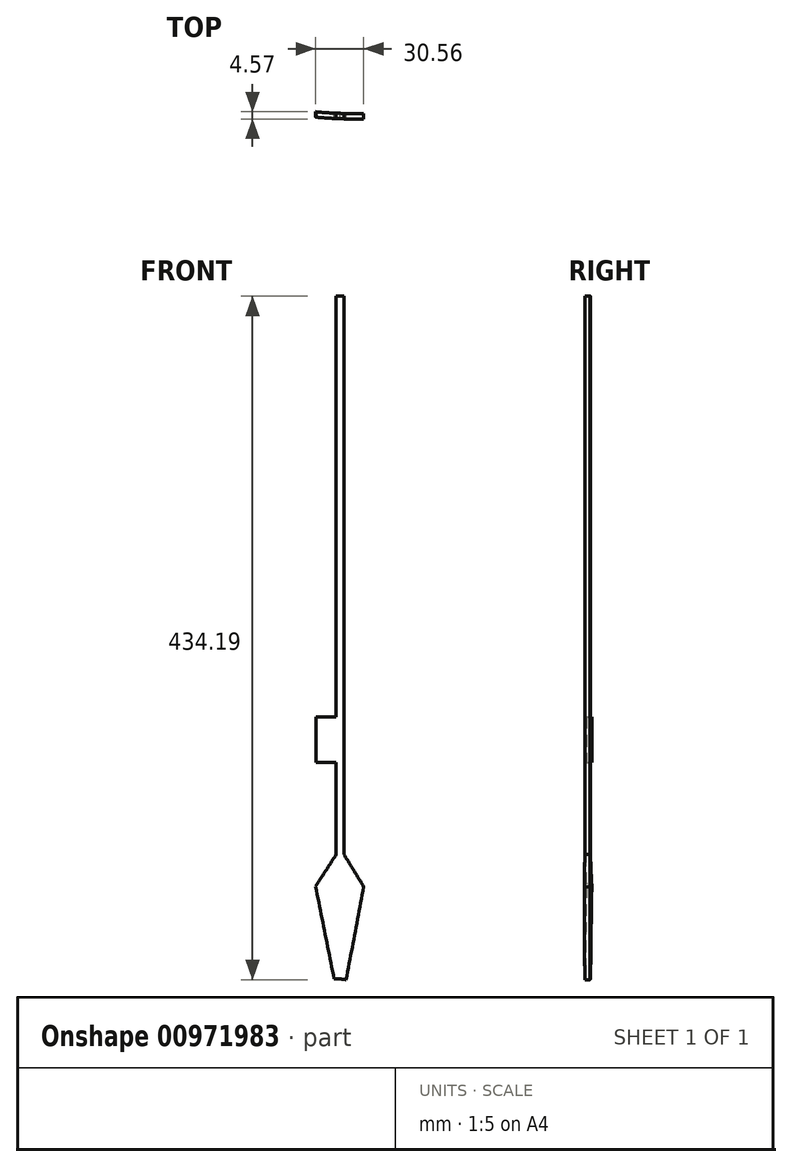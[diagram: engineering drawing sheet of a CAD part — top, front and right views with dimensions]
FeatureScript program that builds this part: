
annotation { "Feature Type Name" : "Feature", "Feature Type Description" : "" }
export const myFeature = defineFeature(function(context is Context, id is Id, definition is map)
    precondition{}
    {
        {
            var Q0;
            Q0=qCreatedBy(makeId("Front.planeOp"),FACE);
            var sketch = newSketch(context, id + "F0", { "sketchPlane" : qUnion([Q0])});
            skLineSegment(sketch, "E0.bottom", {"start": v(-1.3, 3.4) * mm, "end": v(-0.07, 3.4) * mm});
            skLineSegment(sketch, "E0.top", {"start": v(-1.3, -85.17) * mm, "end": v(-0.07, -85.17) * mm});
            skLineSegment(sketch, "E0.left", {"start": v(-1.3, 3.4) * mm, "end": v(-1.3, -85.17) * mm});
            skLineSegment(sketch, "E0.right", {"start": v(-0.07, 3.4) * mm, "end": v(-0.07, -85.17) * mm});
            skLineSegment(sketch, "E1", {"start": v(-1.3, -85.17) * mm, "end": v(-4.57, -90.2) * mm});
            skLineSegment(sketch, "E2", {"start": v(-0.07, -85.17) * mm, "end": v(3.07, -90.29) * mm});
            skLineSegment(sketch, "E3", {"start": v(-4.57, -90.2) * mm, "end": v(-1.63, -104.91) * mm});
            skLineSegment(sketch, "E4", {"start": v(-0.68, -85.17) * mm, "end": v(-0.68, -107.5) * mm});
            skLineSegment(sketch, "E5", {"start": v(3.07, -90.29) * mm, "end": v(0.28, -105.04) * mm});
            skLineSegment(sketch, "E6", {"start": v(-1.63, -104.91) * mm, "end": v(-0.68, -104.91) * mm});
            skLineSegment(sketch, "E7", {"start": v(0.28, -105.04) * mm, "end": v(-0.68, -104.91) * mm});
            skFitSpline(sketch, "E8", {"points": [v(-1.63, -104.91) * mm, v(-0.68, -107.5) * mm, v(0.28, -105.04) * mm], "startDerivative": vector(1.88, -7.65) * mm, "endDerivative": vector(1.95, 7.45) * mm});
            skLineSegment(sketch, "E9", {"start": v(-1.3, -85.17) * mm, "end": v(-1.3, -70.58) * mm});
            skLineSegment(sketch, "E10.bottom", {"start": v(-1.3, -70.58) * mm, "end": v(-4.5, -70.58) * mm});
            skLineSegment(sketch, "E10.top", {"start": v(-1.3, -63.33) * mm, "end": v(-4.5, -63.33) * mm});
            skLineSegment(sketch, "E10.left", {"start": v(-1.3, -70.58) * mm, "end": v(-1.3, -63.33) * mm});
            skLineSegment(sketch, "E10.right", {"start": v(-4.5, -70.58) * mm, "end": v(-4.5, -63.33) * mm});
            skLineSegment(sketch, "E11.bottom", {"start": v(-737.1, 925.24) * mm, "end": v(1003.77, 925.24) * mm});
            skLineSegment(sketch, "E11.top", {"start": v(-737.1, -1334.66) * mm, "end": v(1003.77, -1334.66) * mm});
            skLineSegment(sketch, "E11.left", {"start": v(-737.1, 925.24) * mm, "end": v(-737.1, -1334.66) * mm});
            skLineSegment(sketch, "E11.right", {"start": v(1003.77, 925.24) * mm, "end": v(1003.77, -1334.66) * mm});
            skSolve(sketch);
        }
        {
            var Q0;
            Q0=qCreatedBy(makeId("Top.planeOp"),FACE);
            var sketch = newSketch(context, id + "F1", { "sketchPlane" : qUnion([Q0])});
            skLineSegment(sketch, "E12", {"start": v(2.04, 1.3) * mm, "end": v(2.04, 10.73) * mm});
            skLineSegment(sketch, "E13", {"start": v(2.04, 10.73) * mm, "end": v(45.22, 10.73) * mm});
            skLineSegment(sketch, "E14", {"start": v(45.22, 10.73) * mm, "end": v(43.95, 10.73) * mm});
            skLineSegment(sketch, "E15", {"start": v(2.04, 10.73) * mm, "end": v(-39.87, 10.73) * mm});
            skArc(sketch, "E16", {"start": v(-41.14, 10.73) * mm, "mid": v(2.04, -2.69) * mm, "end": v(45.22, 10.73) * mm});
            skLineSegment(sketch, "E17", {"start": v(2.04, 10.73) * mm, "end": v(2.04, -2.69) * mm});
            skLineSegment(sketch, "E18", {"start": v(-39.87, 10.73) * mm, "end": v(-41.14, 10.73) * mm});
            skLineSegment(sketch, "E19", {"start": v(30.65, 10.73) * mm, "end": v(2.04, 10.73) * mm});
            skLineSegment(sketch, "E20", {"start": v(43.95, 10.73) * mm, "end": v(30.65, 10.73) * mm});
            skArc(sketch, "E21", {"start": v(-39.87, 10.73) * mm, "mid": v(2.04, -1.83) * mm, "end": v(43.95, 10.73) * mm});
            skSolve(sketch);
        }
        {
            var Q0;
            {var subQ0=sQuery(id+"F1.wireOp",EDGE,"E16");var subQ1=sQuery(id+"F1.wireOp",EDGE,"E13");var subQ2=makeQuery(id+"F1.imprint","INTERSECT",VERTEX,{"derivedFrom":[subQ1,subQ0]});Q0=makeQuery(id+"F1.imprint","IMPRINT",FACE,{"disambiguationData":[TD([[makeQuery(id+"F1.imprint","IMPRINT",EDGE,{"disambiguationData":[TD([[subQ2,1.0]])],"derivedFrom":subQ1}),-1.0]])]});}
            var Q1;
            {var subQ0=sQuery(id+"F1.wireOp",EDGE,"E18");Q1=makeQuery(id+"F1.imprint","IMPRINT",FACE,{"disambiguationData":[TD([[makeQuery(id+"F1.imprint","IMPRINT",EDGE,{"derivedFrom":subQ0}),1.0]])]});}
            extrude(context, id + "F2", {"entities" : qUnion([Q0, Q1]), "endBound" : BoundingType.SYMMETRIC, "depth" : 934.72 * mm, "offsetDistance" : 25.4 * mm});
        }
        {
            var Q0;
            {var subQ3=sQuery(id+"F0.wireOp",EDGE,"E7");Q0=makeQuery(id+"F0.imprint","IMPRINT",FACE,{"disambiguationData":[TD([[makeQuery(id+"F0.imprint","IMPRINT",EDGE,{"derivedFrom":subQ3}),1.0]])]});}
            var Q1;
            {var subQ3=sQuery(id+"F0.wireOp",EDGE,"E6");Q1=makeQuery(id+"F0.imprint","IMPRINT",FACE,{"disambiguationData":[TD([[makeQuery(id+"F0.imprint","IMPRINT",EDGE,{"derivedFrom":subQ3}),-1.0]])]});}
            var Q2;
            Q2=makeQuery(id+"F0.imprint","IMPRINT",FACE,{"disambiguationData":[TD([[makeQuery(id+"F0.imprint","IMPRINT",EDGE,{"derivedFrom":sQuery(id+"F0.wireOp",EDGE,"E0.bottom")}),1.0]])]});
            extrude(context, id + "F3", {"entities" : qUnion([Q0, Q1, Q2]), "operationType" : NewBodyOperationType.REMOVE, "endBound" : BoundingType.SYMMETRIC, "depth" : 121.92 * mm, "offsetDistance" : 25.4 * mm});
        }
        {
            var Q0;
            Q0=makeQuery(id+"F2.opExtrude","SWEPT_BODY",BODY,{"disambiguationData":[OSD([sQuery(id+"F1.wireOp",EDGE,"E13"),sQuery(id+"F1.wireOp",EDGE,"E16"),sQuery(id+"F1.wireOp",EDGE,"E18"),sQuery(id+"F1.wireOp",EDGE,"E21")])]});
            var Q1;
            Q1=qCreatedBy(makeId("Origin.pointOp"),VERTEX);
            var Q2;
            Q2=qCreatedBy(makeId("Origin.pointOp"),VERTEX);
            transform(context, id + "F4", {"entities" : qUnion([Q0]), "transformType" : TransformType.SCALE_UNIFORMLY, "scale" : 4, "scalePoint" : qUnion([Q2]), "makeCopy" : false});
        }
    });
